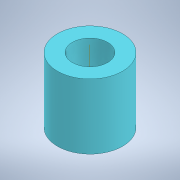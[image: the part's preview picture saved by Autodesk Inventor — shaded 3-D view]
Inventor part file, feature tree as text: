
AUTODESK INVENTOR PART (.ipt)
format: ipt  version: 2021.1 (Build 251245000, 245)  size: 116,224 bytes
history: native  units: in
note: dims shown in document units (in); Inventor stores cm internally (conversion verified against a paired STEP export)
features: sketch x2, extrude x1, helix x1
ambient origin geometry x8: Origin, YZ Plane, XZ Plane, XY Plane, X Axis, Y Axis, Z Axis, Center Point
bodies: Body1 (feature_tree)
feature tree (4):
  extrude  "Extrusion2"  Depth=3.0in
  helix  "Coil3"  [1 undecoded]
  sketch  "Sketch1"  dims[d0=3.0in d10=1.625in d11=3.0in d12=0.0in]
  sketch  "Sketch6"  dims[d31=60.0deg d32=0.3333in d33=2.0in d34=0.3937in d35=0.0in d36=90.0deg d37=90.0deg d38=0.0in d39=0.0in]
note: 1 required parameter value undecoded (feature->parameter linkage not recoverable at this tier; creation-order binding heuristic only, values carry confidence <= 0.55)
